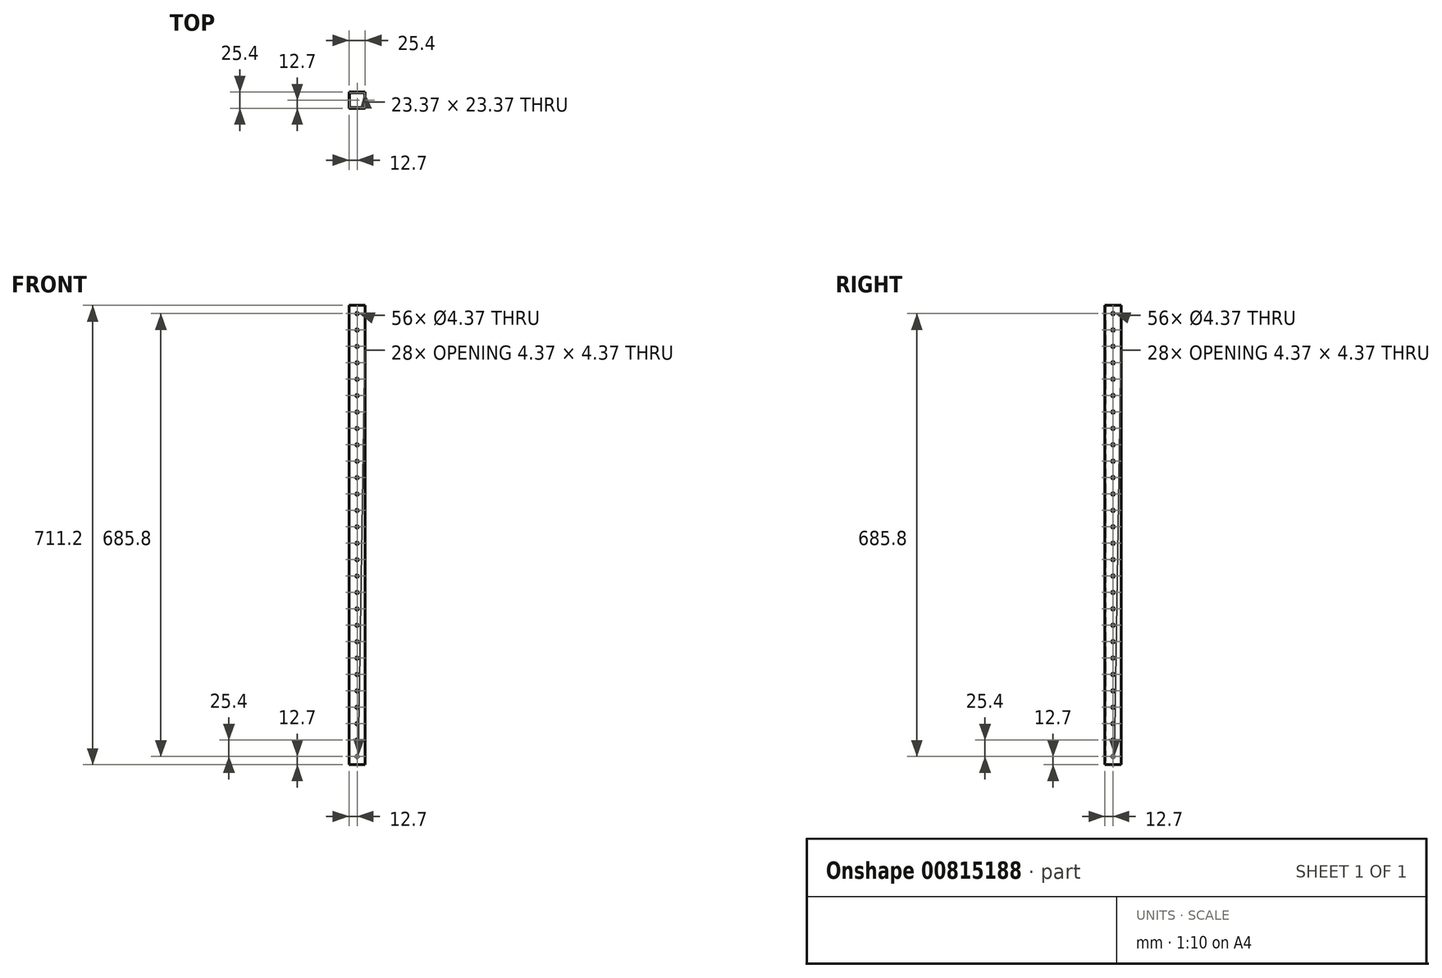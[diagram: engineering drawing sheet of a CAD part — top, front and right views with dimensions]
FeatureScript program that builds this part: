
annotation { "Feature Type Name" : "Feature", "Feature Type Description" : "" }
export const myFeature = defineFeature(function(context is Context, id is Id, definition is map)
    precondition{}
    {
        {
            var Q0;
            Q0=qCreatedBy(makeId("Top.planeOp"),FACE);
            var sketch = newSketch(context, id + "F0", { "sketchPlane" : qUnion([Q0])});
            skLineSegment(sketch, "E0.bottom", {"start": v(0, 0) * mm, "end": v(25.4, 0) * mm});
            skLineSegment(sketch, "E0.top", {"start": v(0, -25.4) * mm, "end": v(25.4, -25.4) * mm});
            skLineSegment(sketch, "E0.left", {"start": v(0, 0) * mm, "end": v(0, -25.4) * mm});
            skLineSegment(sketch, "E0.right", {"start": v(25.4, 0) * mm, "end": v(25.4, -25.4) * mm});
            skLineSegment(sketch, "E1.bottom", {"start": v(1.02, -1.02) * mm, "end": v(24.38, -1.02) * mm});
            skLineSegment(sketch, "E1.top", {"start": v(1.02, -24.38) * mm, "end": v(24.38, -24.38) * mm});
            skLineSegment(sketch, "E1.left", {"start": v(1.02, -1.02) * mm, "end": v(1.02, -24.38) * mm});
            skLineSegment(sketch, "E1.right", {"start": v(24.38, -1.02) * mm, "end": v(24.38, -24.38) * mm});
            skSolve(sketch);
        }
        {
            var Q0;
            Q0=makeQuery(id+"F0.imprint","IMPRINT",FACE,{"disambiguationData":[TD([[makeQuery(id+"F0.imprint","IMPRINT",EDGE,{"derivedFrom":sQuery(id+"F0.wireOp",EDGE,"E0.bottom")}),-1.0]])]});
            extrude(context, id + "F1", {"entities" : qUnion([Q0]), "depth" : 711.2 * mm, "offsetDistance" : 25.4 * mm});
        }
        {
            var Q0;
            Q0=makeQuery(id+"F1.opExtrude","SWEPT_FACE",FACE,{"disambiguationData":[OSD([sQuery(id+"F0.wireOp",EDGE,"E0.top")])]});
            var sketch = newSketch(context, id + "F2", { "sketchPlane" : qUnion([Q0])});
            skCircle(sketch, "E2", {"center": v(12.7, 12.7) * mm, "radius": 2.18 * mm});
            skCircle(sketch, "E3.0.1.0", {"center": v(12.7, 38.1) * mm, "radius": 2.18 * mm});
            skCircle(sketch, "E3.0.2.0", {"center": v(12.7, 63.5) * mm, "radius": 2.18 * mm});
            skCircle(sketch, "E3.0.3.0", {"center": v(12.7, 88.9) * mm, "radius": 2.18 * mm});
            skCircle(sketch, "E3.0.4.0", {"center": v(12.7, 114.3) * mm, "radius": 2.18 * mm});
            skCircle(sketch, "E3.0.5.0", {"center": v(12.7, 139.7) * mm, "radius": 2.18 * mm});
            skCircle(sketch, "E3.0.6.0", {"center": v(12.7, 165.1) * mm, "radius": 2.18 * mm});
            skCircle(sketch, "E3.0.7.0", {"center": v(12.7, 190.5) * mm, "radius": 2.18 * mm});
            skCircle(sketch, "E3.0.8.0", {"center": v(12.7, 215.9) * mm, "radius": 2.18 * mm});
            skCircle(sketch, "E3.0.9.0", {"center": v(12.7, 241.3) * mm, "radius": 2.18 * mm});
            skCircle(sketch, "E3.0.10.0", {"center": v(12.7, 266.7) * mm, "radius": 2.18 * mm});
            skCircle(sketch, "E3.0.11.0", {"center": v(12.7, 292.1) * mm, "radius": 2.18 * mm});
            skCircle(sketch, "E3.0.12.0", {"center": v(12.7, 317.5) * mm, "radius": 2.18 * mm});
            skCircle(sketch, "E3.0.13.0", {"center": v(12.7, 342.9) * mm, "radius": 2.18 * mm});
            skCircle(sketch, "E3.0.14.0", {"center": v(12.7, 368.3) * mm, "radius": 2.18 * mm});
            skCircle(sketch, "E3.0.15.0", {"center": v(12.7, 393.7) * mm, "radius": 2.18 * mm});
            skCircle(sketch, "E3.0.16.0", {"center": v(12.7, 419.1) * mm, "radius": 2.18 * mm});
            skCircle(sketch, "E3.0.17.0", {"center": v(12.7, 444.5) * mm, "radius": 2.18 * mm});
            skCircle(sketch, "E3.0.18.0", {"center": v(12.7, 469.9) * mm, "radius": 2.18 * mm});
            skCircle(sketch, "E3.0.19.0", {"center": v(12.7, 495.3) * mm, "radius": 2.18 * mm});
            skCircle(sketch, "E3.0.20.0", {"center": v(12.7, 520.7) * mm, "radius": 2.18 * mm});
            skCircle(sketch, "E3.0.21.0", {"center": v(12.7, 546.1) * mm, "radius": 2.18 * mm});
            skCircle(sketch, "E3.0.22.0", {"center": v(12.7, 571.5) * mm, "radius": 2.18 * mm});
            skCircle(sketch, "E3.0.23.0", {"center": v(12.7, 596.9) * mm, "radius": 2.18 * mm});
            skCircle(sketch, "E3.0.24.0", {"center": v(12.7, 622.3) * mm, "radius": 2.18 * mm});
            skLineSegment(sketch, "E3.direction1", {"start": v(12.7, 12.7) * mm, "end": v(38.1, 12.7) * mm, "construction": true});
            skLineSegment(sketch, "E3.direction2", {"start": v(12.7, 12.7) * mm, "end": v(12.7, 38.1) * mm, "construction": true});
            skCircle(sketch, "E4.0.0.25", {"center": v(12.7, 647.7) * mm, "radius": 2.18 * mm});
            skCircle(sketch, "E4.0.0.26", {"center": v(12.7, 673.1) * mm, "radius": 2.18 * mm});
            skCircle(sketch, "E4.0.0.27", {"center": v(12.7, 698.5) * mm, "radius": 2.18 * mm});
            skSolve(sketch);
        }
        {
            var Q0;
            Q0=makeQuery(id+"F2.imprint","IMPRINT",FACE,{"disambiguationData":[TD([[makeQuery(id+"F2.imprint","IMPRINT",EDGE,{"derivedFrom":sQuery(id+"F2.wireOp",EDGE,"E2")}),1.0]])]});
            var Q1;
            Q1=makeQuery(id+"F2.imprint","IMPRINT",FACE,{"disambiguationData":[TD([[makeQuery(id+"F2.imprint","IMPRINT",EDGE,{"derivedFrom":sQuery(id+"F2.wireOp",EDGE,"E3.0.1.0")}),1.0]])]});
            var Q2;
            Q2=makeQuery(id+"F2.imprint","IMPRINT",FACE,{"disambiguationData":[TD([[makeQuery(id+"F2.imprint","IMPRINT",EDGE,{"derivedFrom":sQuery(id+"F2.wireOp",EDGE,"E3.0.9.0")}),1.0]])]});
            var Q3;
            Q3=makeQuery(id+"F2.imprint","IMPRINT",FACE,{"disambiguationData":[TD([[makeQuery(id+"F2.imprint","IMPRINT",EDGE,{"derivedFrom":sQuery(id+"F2.wireOp",EDGE,"E3.0.8.0")}),1.0]])]});
            var Q4;
            Q4=makeQuery(id+"F2.imprint","IMPRINT",FACE,{"disambiguationData":[TD([[makeQuery(id+"F2.imprint","IMPRINT",EDGE,{"derivedFrom":sQuery(id+"F2.wireOp",EDGE,"E3.0.7.0")}),1.0]])]});
            var Q5;
            Q5=makeQuery(id+"F2.imprint","IMPRINT",FACE,{"disambiguationData":[TD([[makeQuery(id+"F2.imprint","IMPRINT",EDGE,{"derivedFrom":sQuery(id+"F2.wireOp",EDGE,"E3.0.6.0")}),1.0]])]});
            var Q6;
            Q6=makeQuery(id+"F2.imprint","IMPRINT",FACE,{"disambiguationData":[TD([[makeQuery(id+"F2.imprint","IMPRINT",EDGE,{"derivedFrom":sQuery(id+"F2.wireOp",EDGE,"E3.0.5.0")}),1.0]])]});
            var Q7;
            Q7=makeQuery(id+"F2.imprint","IMPRINT",FACE,{"disambiguationData":[TD([[makeQuery(id+"F2.imprint","IMPRINT",EDGE,{"derivedFrom":sQuery(id+"F2.wireOp",EDGE,"E3.0.4.0")}),1.0]])]});
            var Q8;
            Q8=makeQuery(id+"F2.imprint","IMPRINT",FACE,{"disambiguationData":[TD([[makeQuery(id+"F2.imprint","IMPRINT",EDGE,{"derivedFrom":sQuery(id+"F2.wireOp",EDGE,"E3.0.3.0")}),1.0]])]});
            var Q9;
            Q9=makeQuery(id+"F2.imprint","IMPRINT",FACE,{"disambiguationData":[TD([[makeQuery(id+"F2.imprint","IMPRINT",EDGE,{"derivedFrom":sQuery(id+"F2.wireOp",EDGE,"E3.0.2.0")}),1.0]])]});
            var Q10;
            Q10=makeQuery(id+"F2.imprint","IMPRINT",FACE,{"disambiguationData":[TD([[makeQuery(id+"F2.imprint","IMPRINT",EDGE,{"derivedFrom":sQuery(id+"F2.wireOp",EDGE,"E3.0.10.0")}),1.0]])]});
            var Q11;
            Q11=makeQuery(id+"F2.imprint","IMPRINT",FACE,{"disambiguationData":[TD([[makeQuery(id+"F2.imprint","IMPRINT",EDGE,{"derivedFrom":sQuery(id+"F2.wireOp",EDGE,"E3.0.11.0")}),1.0]])]});
            var Q12;
            Q12=makeQuery(id+"F2.imprint","IMPRINT",FACE,{"disambiguationData":[TD([[makeQuery(id+"F2.imprint","IMPRINT",EDGE,{"derivedFrom":sQuery(id+"F2.wireOp",EDGE,"E3.0.12.0")}),1.0]])]});
            var Q13;
            Q13=makeQuery(id+"F2.imprint","IMPRINT",FACE,{"disambiguationData":[TD([[makeQuery(id+"F2.imprint","IMPRINT",EDGE,{"derivedFrom":sQuery(id+"F2.wireOp",EDGE,"E3.0.13.0")}),1.0]])]});
            var Q14;
            Q14=makeQuery(id+"F2.imprint","IMPRINT",FACE,{"disambiguationData":[TD([[makeQuery(id+"F2.imprint","IMPRINT",EDGE,{"derivedFrom":sQuery(id+"F2.wireOp",EDGE,"E3.0.14.0")}),1.0]])]});
            var Q15;
            Q15=makeQuery(id+"F2.imprint","IMPRINT",FACE,{"disambiguationData":[TD([[makeQuery(id+"F2.imprint","IMPRINT",EDGE,{"derivedFrom":sQuery(id+"F2.wireOp",EDGE,"E3.0.15.0")}),1.0]])]});
            var Q16;
            Q16=makeQuery(id+"F2.imprint","IMPRINT",FACE,{"disambiguationData":[TD([[makeQuery(id+"F2.imprint","IMPRINT",EDGE,{"derivedFrom":sQuery(id+"F2.wireOp",EDGE,"E3.0.16.0")}),1.0]])]});
            var Q17;
            Q17=makeQuery(id+"F2.imprint","IMPRINT",FACE,{"disambiguationData":[TD([[makeQuery(id+"F2.imprint","IMPRINT",EDGE,{"derivedFrom":sQuery(id+"F2.wireOp",EDGE,"E3.0.17.0")}),1.0]])]});
            var Q18;
            Q18=makeQuery(id+"F2.imprint","IMPRINT",FACE,{"disambiguationData":[TD([[makeQuery(id+"F2.imprint","IMPRINT",EDGE,{"derivedFrom":sQuery(id+"F2.wireOp",EDGE,"E3.0.18.0")}),1.0]])]});
            var Q19;
            Q19=makeQuery(id+"F2.imprint","IMPRINT",FACE,{"disambiguationData":[TD([[makeQuery(id+"F2.imprint","IMPRINT",EDGE,{"derivedFrom":sQuery(id+"F2.wireOp",EDGE,"E3.0.19.0")}),1.0]])]});
            var Q20;
            Q20=makeQuery(id+"F2.imprint","IMPRINT",FACE,{"disambiguationData":[TD([[makeQuery(id+"F2.imprint","IMPRINT",EDGE,{"derivedFrom":sQuery(id+"F2.wireOp",EDGE,"E3.0.20.0")}),1.0]])]});
            var Q21;
            Q21=makeQuery(id+"F2.imprint","IMPRINT",FACE,{"disambiguationData":[TD([[makeQuery(id+"F2.imprint","IMPRINT",EDGE,{"derivedFrom":sQuery(id+"F2.wireOp",EDGE,"E3.0.21.0")}),1.0]])]});
            var Q22;
            Q22=makeQuery(id+"F2.imprint","IMPRINT",FACE,{"disambiguationData":[TD([[makeQuery(id+"F2.imprint","IMPRINT",EDGE,{"derivedFrom":sQuery(id+"F2.wireOp",EDGE,"E3.0.22.0")}),1.0]])]});
            var Q23;
            Q23=makeQuery(id+"F2.imprint","IMPRINT",FACE,{"disambiguationData":[TD([[makeQuery(id+"F2.imprint","IMPRINT",EDGE,{"derivedFrom":sQuery(id+"F2.wireOp",EDGE,"E3.0.23.0")}),1.0]])]});
            var Q24;
            Q24=makeQuery(id+"F2.imprint","IMPRINT",FACE,{"disambiguationData":[TD([[makeQuery(id+"F2.imprint","IMPRINT",EDGE,{"derivedFrom":sQuery(id+"F2.wireOp",EDGE,"E3.0.24.0")}),1.0]])]});
            var Q25;
            Q25=makeQuery(id+"F2.imprint","IMPRINT",FACE,{"disambiguationData":[TD([[makeQuery(id+"F2.imprint","IMPRINT",EDGE,{"derivedFrom":sQuery(id+"F2.wireOp",EDGE,"E4.0.0.25")}),1.0]])]});
            var Q26;
            Q26=makeQuery(id+"F2.imprint","IMPRINT",FACE,{"disambiguationData":[TD([[makeQuery(id+"F2.imprint","IMPRINT",EDGE,{"derivedFrom":sQuery(id+"F2.wireOp",EDGE,"E4.0.0.26")}),1.0]])]});
            var Q27;
            Q27=makeQuery(id+"F2.imprint","IMPRINT",FACE,{"disambiguationData":[TD([[makeQuery(id+"F2.imprint","IMPRINT",EDGE,{"derivedFrom":sQuery(id+"F2.wireOp",EDGE,"E4.0.0.27")}),1.0]])]});
            extrude(context, id + "F3", {"entities" : qUnion([Q0, Q1, Q2, Q3, Q4, Q5, Q6, Q7, Q8, Q9, Q10, Q11, Q12, Q13, Q14, Q15, Q16, Q17, Q18, Q19, Q20, Q21, Q22, Q23, Q24, Q25, Q26, Q27]), "operationType" : NewBodyOperationType.REMOVE, "oppositeDirection" : true, "depth" : 25.4 * mm, "offsetDistance" : 25.4 * mm});
        }
        {
            var Q0;
            Q0=makeQuery(id+"F1.opExtrude","SWEPT_FACE",FACE,{"disambiguationData":[OSD([sQuery(id+"F0.wireOp",EDGE,"E0.left")])]});
            var sketch = newSketch(context, id + "F4", { "sketchPlane" : qUnion([Q0])});
            skCircle(sketch, "E5", {"center": v(12.7, 12.7) * mm, "radius": 2.18 * mm});
            skCircle(sketch, "E6.0.1.0", {"center": v(12.7, 38.1) * mm, "radius": 2.18 * mm});
            skCircle(sketch, "E6.0.2.0", {"center": v(12.7, 63.5) * mm, "radius": 2.18 * mm});
            skCircle(sketch, "E6.0.3.0", {"center": v(12.7, 88.9) * mm, "radius": 2.18 * mm});
            skCircle(sketch, "E6.0.4.0", {"center": v(12.7, 114.3) * mm, "radius": 2.18 * mm});
            skCircle(sketch, "E6.0.5.0", {"center": v(12.7, 139.7) * mm, "radius": 2.18 * mm});
            skCircle(sketch, "E6.0.6.0", {"center": v(12.7, 165.1) * mm, "radius": 2.18 * mm});
            skCircle(sketch, "E6.0.7.0", {"center": v(12.7, 190.5) * mm, "radius": 2.18 * mm});
            skCircle(sketch, "E6.0.8.0", {"center": v(12.7, 215.9) * mm, "radius": 2.18 * mm});
            skCircle(sketch, "E6.0.9.0", {"center": v(12.7, 241.3) * mm, "radius": 2.18 * mm});
            skCircle(sketch, "E6.0.10.0", {"center": v(12.7, 266.7) * mm, "radius": 2.18 * mm});
            skCircle(sketch, "E6.0.11.0", {"center": v(12.7, 292.1) * mm, "radius": 2.18 * mm});
            skCircle(sketch, "E6.0.12.0", {"center": v(12.7, 317.5) * mm, "radius": 2.18 * mm});
            skCircle(sketch, "E6.0.13.0", {"center": v(12.7, 342.9) * mm, "radius": 2.18 * mm});
            skCircle(sketch, "E6.0.14.0", {"center": v(12.7, 368.3) * mm, "radius": 2.18 * mm});
            skCircle(sketch, "E6.0.15.0", {"center": v(12.7, 393.7) * mm, "radius": 2.18 * mm});
            skCircle(sketch, "E6.0.16.0", {"center": v(12.7, 419.1) * mm, "radius": 2.18 * mm});
            skCircle(sketch, "E6.0.17.0", {"center": v(12.7, 444.5) * mm, "radius": 2.18 * mm});
            skCircle(sketch, "E6.0.18.0", {"center": v(12.7, 469.9) * mm, "radius": 2.18 * mm});
            skCircle(sketch, "E6.0.19.0", {"center": v(12.7, 495.3) * mm, "radius": 2.18 * mm});
            skCircle(sketch, "E6.0.20.0", {"center": v(12.7, 520.7) * mm, "radius": 2.18 * mm});
            skCircle(sketch, "E6.0.21.0", {"center": v(12.7, 546.1) * mm, "radius": 2.18 * mm});
            skCircle(sketch, "E6.0.22.0", {"center": v(12.7, 571.5) * mm, "radius": 2.18 * mm});
            skCircle(sketch, "E6.0.23.0", {"center": v(12.7, 596.9) * mm, "radius": 2.18 * mm});
            skCircle(sketch, "E6.0.24.0", {"center": v(12.7, 622.3) * mm, "radius": 2.18 * mm});
            skLineSegment(sketch, "E6.direction1", {"start": v(12.7, 12.7) * mm, "end": v(38.1, 12.7) * mm, "construction": true});
            skLineSegment(sketch, "E6.direction2", {"start": v(12.7, 12.7) * mm, "end": v(12.7, 38.1) * mm, "construction": true});
            skCircle(sketch, "E7.0.0.25", {"center": v(12.7, 647.7) * mm, "radius": 2.18 * mm});
            skCircle(sketch, "E7.0.0.26", {"center": v(12.7, 673.1) * mm, "radius": 2.18 * mm});
            skCircle(sketch, "E7.0.0.27", {"center": v(12.7, 698.5) * mm, "radius": 2.18 * mm});
            skSolve(sketch);
        }
        {
            var Q0;
            Q0=makeQuery(id+"F4.imprint","IMPRINT",FACE,{"disambiguationData":[TD([[makeQuery(id+"F4.imprint","IMPRINT",EDGE,{"derivedFrom":sQuery(id+"F4.wireOp",EDGE,"E5")}),1.0]])]});
            var Q1;
            Q1=makeQuery(id+"F4.imprint","IMPRINT",FACE,{"disambiguationData":[TD([[makeQuery(id+"F4.imprint","IMPRINT",EDGE,{"derivedFrom":sQuery(id+"F4.wireOp",EDGE,"E6.0.1.0")}),1.0]])]});
            var Q2;
            Q2=makeQuery(id+"F4.imprint","IMPRINT",FACE,{"disambiguationData":[TD([[makeQuery(id+"F4.imprint","IMPRINT",EDGE,{"derivedFrom":sQuery(id+"F4.wireOp",EDGE,"E6.0.2.0")}),1.0]])]});
            var Q3;
            Q3=makeQuery(id+"F4.imprint","IMPRINT",FACE,{"disambiguationData":[TD([[makeQuery(id+"F4.imprint","IMPRINT",EDGE,{"derivedFrom":sQuery(id+"F4.wireOp",EDGE,"E6.0.3.0")}),1.0]])]});
            var Q4;
            Q4=makeQuery(id+"F4.imprint","IMPRINT",FACE,{"disambiguationData":[TD([[makeQuery(id+"F4.imprint","IMPRINT",EDGE,{"derivedFrom":sQuery(id+"F4.wireOp",EDGE,"E6.0.4.0")}),1.0]])]});
            var Q5;
            Q5=makeQuery(id+"F4.imprint","IMPRINT",FACE,{"disambiguationData":[TD([[makeQuery(id+"F4.imprint","IMPRINT",EDGE,{"derivedFrom":sQuery(id+"F4.wireOp",EDGE,"E6.0.5.0")}),1.0]])]});
            var Q6;
            Q6=makeQuery(id+"F4.imprint","IMPRINT",FACE,{"disambiguationData":[TD([[makeQuery(id+"F4.imprint","IMPRINT",EDGE,{"derivedFrom":sQuery(id+"F4.wireOp",EDGE,"E6.0.6.0")}),1.0]])]});
            var Q7;
            Q7=makeQuery(id+"F4.imprint","IMPRINT",FACE,{"disambiguationData":[TD([[makeQuery(id+"F4.imprint","IMPRINT",EDGE,{"derivedFrom":sQuery(id+"F4.wireOp",EDGE,"E6.0.7.0")}),1.0]])]});
            var Q8;
            Q8=makeQuery(id+"F4.imprint","IMPRINT",FACE,{"disambiguationData":[TD([[makeQuery(id+"F4.imprint","IMPRINT",EDGE,{"derivedFrom":sQuery(id+"F4.wireOp",EDGE,"E6.0.8.0")}),1.0]])]});
            var Q9;
            Q9=makeQuery(id+"F4.imprint","IMPRINT",FACE,{"disambiguationData":[TD([[makeQuery(id+"F4.imprint","IMPRINT",EDGE,{"derivedFrom":sQuery(id+"F4.wireOp",EDGE,"E6.0.9.0")}),1.0]])]});
            var Q10;
            Q10=makeQuery(id+"F4.imprint","IMPRINT",FACE,{"disambiguationData":[TD([[makeQuery(id+"F4.imprint","IMPRINT",EDGE,{"derivedFrom":sQuery(id+"F4.wireOp",EDGE,"E6.0.10.0")}),1.0]])]});
            var Q11;
            Q11=makeQuery(id+"F4.imprint","IMPRINT",FACE,{"disambiguationData":[TD([[makeQuery(id+"F4.imprint","IMPRINT",EDGE,{"derivedFrom":sQuery(id+"F4.wireOp",EDGE,"E6.0.11.0")}),1.0]])]});
            var Q12;
            Q12=makeQuery(id+"F4.imprint","IMPRINT",FACE,{"disambiguationData":[TD([[makeQuery(id+"F4.imprint","IMPRINT",EDGE,{"derivedFrom":sQuery(id+"F4.wireOp",EDGE,"E6.0.12.0")}),1.0]])]});
            var Q13;
            Q13=makeQuery(id+"F4.imprint","IMPRINT",FACE,{"disambiguationData":[TD([[makeQuery(id+"F4.imprint","IMPRINT",EDGE,{"derivedFrom":sQuery(id+"F4.wireOp",EDGE,"E6.0.13.0")}),1.0]])]});
            var Q14;
            Q14=makeQuery(id+"F4.imprint","IMPRINT",FACE,{"disambiguationData":[TD([[makeQuery(id+"F4.imprint","IMPRINT",EDGE,{"derivedFrom":sQuery(id+"F4.wireOp",EDGE,"E6.0.14.0")}),1.0]])]});
            var Q15;
            Q15=makeQuery(id+"F4.imprint","IMPRINT",FACE,{"disambiguationData":[TD([[makeQuery(id+"F4.imprint","IMPRINT",EDGE,{"derivedFrom":sQuery(id+"F4.wireOp",EDGE,"E6.0.15.0")}),1.0]])]});
            var Q16;
            Q16=makeQuery(id+"F4.imprint","IMPRINT",FACE,{"disambiguationData":[TD([[makeQuery(id+"F4.imprint","IMPRINT",EDGE,{"derivedFrom":sQuery(id+"F4.wireOp",EDGE,"E6.0.16.0")}),1.0]])]});
            var Q17;
            Q17=makeQuery(id+"F4.imprint","IMPRINT",FACE,{"disambiguationData":[TD([[makeQuery(id+"F4.imprint","IMPRINT",EDGE,{"derivedFrom":sQuery(id+"F4.wireOp",EDGE,"E6.0.17.0")}),1.0]])]});
            var Q18;
            Q18=makeQuery(id+"F4.imprint","IMPRINT",FACE,{"disambiguationData":[TD([[makeQuery(id+"F4.imprint","IMPRINT",EDGE,{"derivedFrom":sQuery(id+"F4.wireOp",EDGE,"E6.0.21.0")}),1.0]])]});
            var Q19;
            Q19=makeQuery(id+"F4.imprint","IMPRINT",FACE,{"disambiguationData":[TD([[makeQuery(id+"F4.imprint","IMPRINT",EDGE,{"derivedFrom":sQuery(id+"F4.wireOp",EDGE,"E6.0.20.0")}),1.0]])]});
            var Q20;
            Q20=makeQuery(id+"F4.imprint","IMPRINT",FACE,{"disambiguationData":[TD([[makeQuery(id+"F4.imprint","IMPRINT",EDGE,{"derivedFrom":sQuery(id+"F4.wireOp",EDGE,"E6.0.19.0")}),1.0]])]});
            var Q21;
            Q21=makeQuery(id+"F4.imprint","IMPRINT",FACE,{"disambiguationData":[TD([[makeQuery(id+"F4.imprint","IMPRINT",EDGE,{"derivedFrom":sQuery(id+"F4.wireOp",EDGE,"E6.0.18.0")}),1.0]])]});
            var Q22;
            Q22=makeQuery(id+"F4.imprint","IMPRINT",FACE,{"disambiguationData":[TD([[makeQuery(id+"F4.imprint","IMPRINT",EDGE,{"derivedFrom":sQuery(id+"F4.wireOp",EDGE,"E6.0.22.0")}),1.0]])]});
            var Q23;
            Q23=makeQuery(id+"F4.imprint","IMPRINT",FACE,{"disambiguationData":[TD([[makeQuery(id+"F4.imprint","IMPRINT",EDGE,{"derivedFrom":sQuery(id+"F4.wireOp",EDGE,"E6.0.23.0")}),1.0]])]});
            var Q24;
            Q24=makeQuery(id+"F4.imprint","IMPRINT",FACE,{"disambiguationData":[TD([[makeQuery(id+"F4.imprint","IMPRINT",EDGE,{"derivedFrom":sQuery(id+"F4.wireOp",EDGE,"E6.0.24.0")}),1.0]])]});
            var Q25;
            Q25=makeQuery(id+"F4.imprint","IMPRINT",FACE,{"disambiguationData":[TD([[makeQuery(id+"F4.imprint","IMPRINT",EDGE,{"derivedFrom":sQuery(id+"F4.wireOp",EDGE,"E7.0.0.25")}),1.0]])]});
            var Q26;
            Q26=makeQuery(id+"F4.imprint","IMPRINT",FACE,{"disambiguationData":[TD([[makeQuery(id+"F4.imprint","IMPRINT",EDGE,{"derivedFrom":sQuery(id+"F4.wireOp",EDGE,"E7.0.0.26")}),1.0]])]});
            var Q27;
            Q27=makeQuery(id+"F4.imprint","IMPRINT",FACE,{"disambiguationData":[TD([[makeQuery(id+"F4.imprint","IMPRINT",EDGE,{"derivedFrom":sQuery(id+"F4.wireOp",EDGE,"E7.0.0.27")}),1.0]])]});
            extrude(context, id + "F5", {"entities" : qUnion([Q0, Q1, Q2, Q3, Q4, Q5, Q6, Q7, Q8, Q9, Q10, Q11, Q12, Q13, Q14, Q15, Q16, Q17, Q18, Q19, Q20, Q21, Q22, Q23, Q24, Q25, Q26, Q27]), "operationType" : NewBodyOperationType.REMOVE, "oppositeDirection" : true, "depth" : 25.4 * mm, "offsetDistance" : 25.4 * mm});
        }
    });
